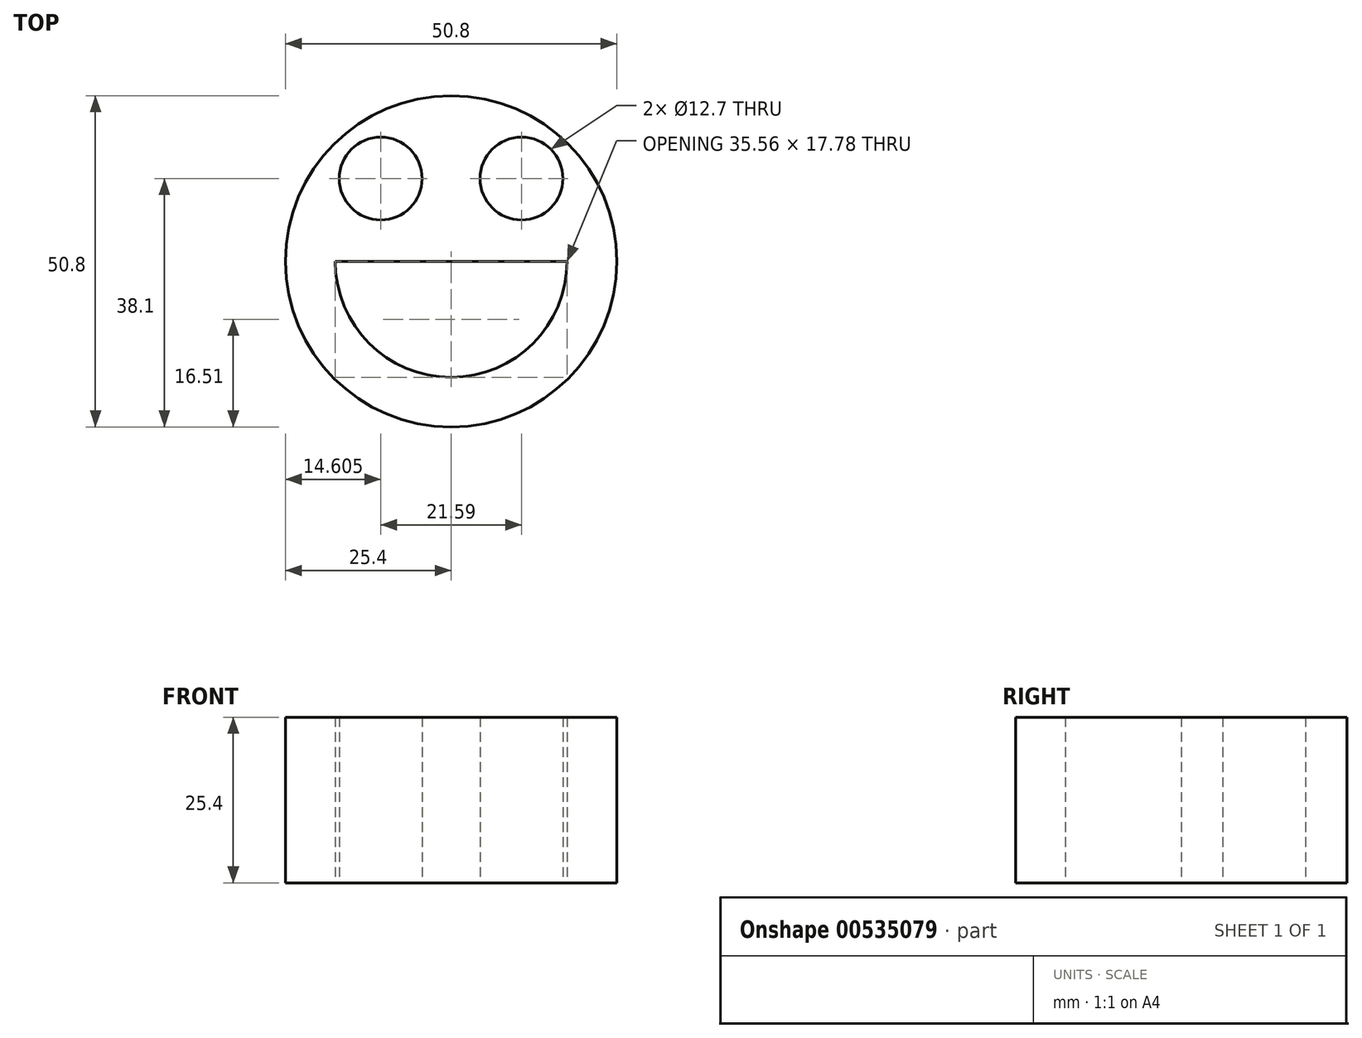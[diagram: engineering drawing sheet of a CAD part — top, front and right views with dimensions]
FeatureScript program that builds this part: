
annotation { "Feature Type Name" : "Feature", "Feature Type Description" : "" }
export const myFeature = defineFeature(function(context is Context, id is Id, definition is map)
    precondition{}
    {
        {
            var Q0;
            Q0=qCreatedBy(makeId("Top.planeOp"),FACE);
            var sketch = newSketch(context, id + "F0", { "sketchPlane" : qUnion([Q0])});
            skCircle(sketch, "E0", {"center": v(0, 0) * mm, "radius": 25.4 * mm});
            skCircle(sketch, "E1", {"center": v(10.8, 12.7) * mm, "radius": 6.35 * mm});
            skCircle(sketch, "E2", {"center": v(-10.8, 12.7) * mm, "radius": 6.35 * mm});
            skArc(sketch, "E3", {"start": v(17.78, 0) * mm, "mid": v(0, -17.78) * mm, "end": v(-17.78, 0) * mm});
            skLineSegment(sketch, "E4", {"start": v(-17.78, 0) * mm, "end": v(17.78, 0) * mm});
            skSolve(sketch);
        }
        {
            var Q0;
            Q0 = qSketchRegion(id + "F0", true);
            extrude(context, id + "F1", {"entities" : qUnion([Q0]), "depth" : 25.4 * mm, "offsetDistance" : 25.4 * mm});
        }
    });
